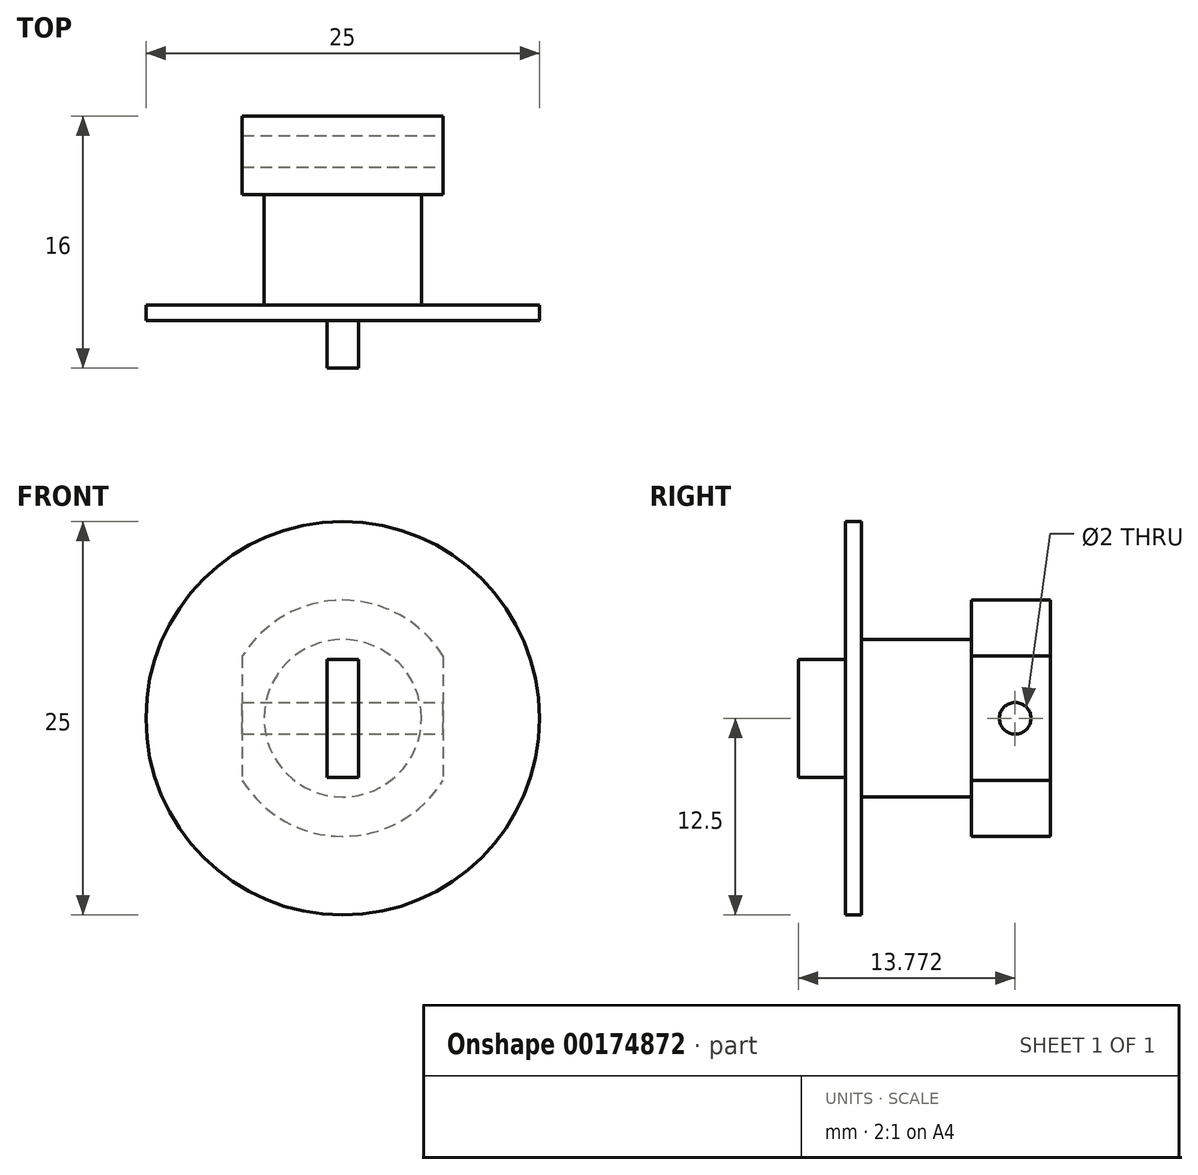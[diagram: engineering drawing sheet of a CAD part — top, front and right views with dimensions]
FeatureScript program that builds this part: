
annotation { "Feature Type Name" : "Feature", "Feature Type Description" : "" }
export const myFeature = defineFeature(function(context is Context, id is Id, definition is map)
    precondition{}
    {
        {
            var Q0;
            Q0=qCreatedBy(makeId("Front.planeOp"),FACE);
            var sketch = newSketch(context, id + "F0", { "sketchPlane" : qUnion([Q0])});
            skCircle(sketch, "E0", {"center": v(0, 0) * mm, "radius": 7.5 * mm});
            skSolve(sketch);
        }
        {
            var Q0;
            Q0 = qSketchRegion(id + "F0", true);
            extrude(context, id + "F1", {"entities" : qUnion([Q0]), "depth" : 5 * mm});
        }
        {
            var Q0;
            Q0=makeQuery(id+"F1.opExtrude","CAP_FACE",FACE,{"disambiguationData":[OSD([sQuery(id+"F0.wireOp",EDGE,"E0")])],"isStart":false});
            var sketch = newSketch(context, id + "F2", { "sketchPlane" : qUnion([Q0])});
            skCircle(sketch, "E1", {"center": v(0, 0) * mm, "radius": 5 * mm});
            skSolve(sketch);
        }
        {
            var Q0;
            Q0 = qSketchRegion(id + "F2", true);
            extrude(context, id + "F3", {"entities" : qUnion([Q0]), "operationType" : NewBodyOperationType.ADD, "depth" : 7 * mm});
        }
        {
            var Q0;
            Q0=makeQuery(id+"F3.opExtrude","CAP_FACE",FACE,{"disambiguationData":[OSD([sQuery(id+"F2.wireOp",EDGE,"E1")])],"isStart":false});
            var sketch = newSketch(context, id + "F4", { "sketchPlane" : qUnion([Q0])});
            skCircle(sketch, "E2", {"center": v(0, 0) * mm, "radius": 12.5 * mm});
            skSolve(sketch);
        }
        {
            var Q0;
            Q0 = qSketchRegion(id + "F4", true);
            extrude(context, id + "F5", {"entities" : qUnion([Q0]), "operationType" : NewBodyOperationType.ADD, "depth" : 1 * mm});
        }
        {
            var Q0;
            Q0=makeQuery(id+"F5.opExtrude","CAP_FACE",FACE,{"disambiguationData":[OSD([sQuery(id+"F4.wireOp",EDGE,"E2")])],"isStart":false});
            var sketch = newSketch(context, id + "F6", { "sketchPlane" : qUnion([Q0])});
            skLineSegment(sketch, "E3.bottom", {"start": v(1, 3.75) * mm, "end": v(-1, 3.75) * mm});
            skLineSegment(sketch, "E3.top", {"start": v(1, -3.75) * mm, "end": v(-1, -3.75) * mm});
            skLineSegment(sketch, "E3.left", {"start": v(1, 3.75) * mm, "end": v(1, -3.75) * mm});
            skLineSegment(sketch, "E3.right", {"start": v(-1, 3.75) * mm, "end": v(-1, -3.75) * mm});
            skPoint(sketch, "E3.middle", {"position": v(0, 0) * mm});
            skSolve(sketch);
        }
        {
            var Q0;
            Q0 = qSketchRegion(id + "F6", true);
            extrude(context, id + "F7", {"entities" : qUnion([Q0]), "operationType" : NewBodyOperationType.ADD, "depth" : 3 * mm});
        }
        {
            var Q0;
            Q0=makeQuery(id+"F1.opExtrude","CAP_FACE",FACE,{"disambiguationData":[OSD([sQuery(id+"F0.wireOp",EDGE,"E0")])],"isStart":true});
            var sketch = newSketch(context, id + "F8", { "sketchPlane" : qUnion([Q0])});
            skLineSegment(sketch, "E4.left", {"start": v(-6.38, 3.95) * mm, "end": v(-6.38, -3.95) * mm});
            skLineSegment(sketch, "E4.right", {"start": v(6.38, 3.95) * mm, "end": v(6.38, -3.95) * mm});
            skPoint(sketch, "E4.middle", {"position": v(0, 0) * mm});
            skArc(sketch, "E5", {"start": v(-6.38, 3.95) * mm, "mid": v(-7.5, 0) * mm, "end": v(-6.38, -3.95) * mm});
            skArc(sketch, "E6.trimOffspring", {"start": v(6.38, -3.95) * mm, "mid": v(7.5, 0) * mm, "end": v(6.38, 3.95) * mm});
            skSolve(sketch);
        }
        {
            var Q0;
            Q0 = qSketchRegion(id + "F8", true);
            extrude(context, id + "F9", {"entities" : qUnion([Q0]), "operationType" : NewBodyOperationType.REMOVE, "oppositeDirection" : true, "depth" : 5 * mm});
        }
        {
            var Q0;
            Q0=makeQuery(id+"F9.boolean.opBoolean","COPY",FACE,{"derivedFrom":makeQuery(id+"F9.opExtrude","SWEPT_FACE",FACE,{"disambiguationData":[OSD([sQuery(id+"F8.wireOp",EDGE,"E4.left")])]})});
            var sketch = newSketch(context, id + "F10", { "sketchPlane" : qUnion([Q0])});
            skCircle(sketch, "E7", {"center": v(-2.23, 0) * mm, "radius": 1 * mm});
            skSolve(sketch);
        }
        {
            var Q0;
            Q0 = qSketchRegion(id + "F10", true);
            extrude(context, id + "F11", {"entities" : qUnion([Q0]), "operationType" : NewBodyOperationType.REMOVE, "oppositeDirection" : true, "depth" : 25 * mm});
        }
    });
